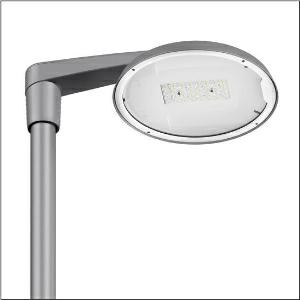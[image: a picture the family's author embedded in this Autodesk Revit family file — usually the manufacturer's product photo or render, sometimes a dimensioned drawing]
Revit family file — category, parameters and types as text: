
# Revit family: dl_r__50_iq_mini___st0_5a_5xa248b41f08ke_519f
name_source: partatom
category: Lighting Fixtures
units: mm (PartAtom-declared; Revit-internal decimal feet)

## family parameters
Cut with Voids When Loaded = No
Host = Face
Light Source = No
Part Type = Normal
Room Calculation Point = No
Round Connector Dimension = Use Diameter
Shared = No

## types (1)
- --- (1 x LED, 5510 lm, 30.8 W, 4000K)
    Apparent Load = 31 VA
    CIE Flux Codes = 43 76 97 100 100
    Color Rendering = 70
    Color Temperature = 4000K
    Default Elevation = 1800 mm
    Description = DL® 50 iQ mini, mast luminaire, primary light control with lens, of PMMA, primary optical cover: cover, of toughened safety glass, transparent, light distribution: ST0.5a, light emission: direct distribution, primary light characteristic: asymmetric, installation type: side-entry, post-top, LED, High Power LED, rated luminous flux: 5.510lm, luminous efficacy: 179lm/W, light colour: 740, colour temperature: 4000K, control: optimised constant luminous flux control (CLO 2.0), Desk-Remote (wireless, voltage-free reading and setting of iQ features in the workshop via application-optimized NFC function/RFID function), Light-Fading, Smart-Wire, Night-Set, Lumen-Switch, Temp-Guard, Auto-Match, Street-Remote, mains connection: 230..240V, AC, 50/60Hz, connection cable pre-assembled, cable length: 6,5m, start of lifetime: 31W, end of service life: 32W, reduction: 15W, luminaire housing, of diecast aluminium, powder-coated, Siteco® metallic grey (DB 702S), inclination adjustable: 0°, 5°, 10° (post-top) | 0°, -5°, -10°, -15° (side-entry), please order mast post-top element or mast side-entry element separately, diameter: 500mm, height: 115mm, post-top: for spigot size d x l = 76 x 100mm; with reducer (optional accessory) 60 x 100mm | side-entry: for spigot size d x l = 60 x 100mm; with reducer (optional accessory) 42 x 100mm, protection rating (complete): IP66, insulation class (complete): insulation class II (safety insulation), certification: CE, ENEC, VDE, impact resistance: IK08, permissible operating ambient temperature for outdoor applications: -25..+40°C, standard-compliant lighting for roads and squares, packaging unit: 1 piece

Light Distribution: ST0.5a
    Height = 115 mm
    Lamp = 1 x LED
    Lamp Light Flux = 5510 lm
    Lamp Power = 30.8 W
    Lamp count = 1
    Length = 500 mm
    Luminous efficacy = 179 lm/W
    Manufacturer = Siteco
    ModVariant = No
    Model = 5XA248B41F08KE
    Number of Poles = 1
    OnlyDefault = Yes
    Power Factor = 1
    Product Name = DL® 50 iQ mini | ST0.5a
    Product group = mast luminaire | pylon top
    ProductGroupID = 6100
    Protection Class = Protection class II
    Protection Degree = IP 66
    RLX_Detail_Level = 1
    RLX_Emergency_Light_Flux = 0 lm
    RLX_Emergency_Type = 0
    RLX_Emergency_Type_DB = No
    RlxData = <blob elided: 126981 chars, md5=da775406>
    Socket = socket
    Standby Power = 0 W
    System Light Flux = 5510 lm
    System Power = 31 W
    Type Comments = factory setting: luminous flux: 100 % | dim-lin: 254 | 329 mA
    Type Image = l_1251794.jpg
    URL = http://relux.com
    VarID = @adj_092327
    Voltage = 0 V
    Weight = 0.00 kg
    Width = 0 mm  [stored 0 ft]

note: [stored X ft] marks values corroborated as IEEE doubles in the binary element streams (Revit-internal decimal feet)

## geometry (parser evidence)
native form markers: Blend x4, Sweep x9
no freeform markers — native parametric forms only
